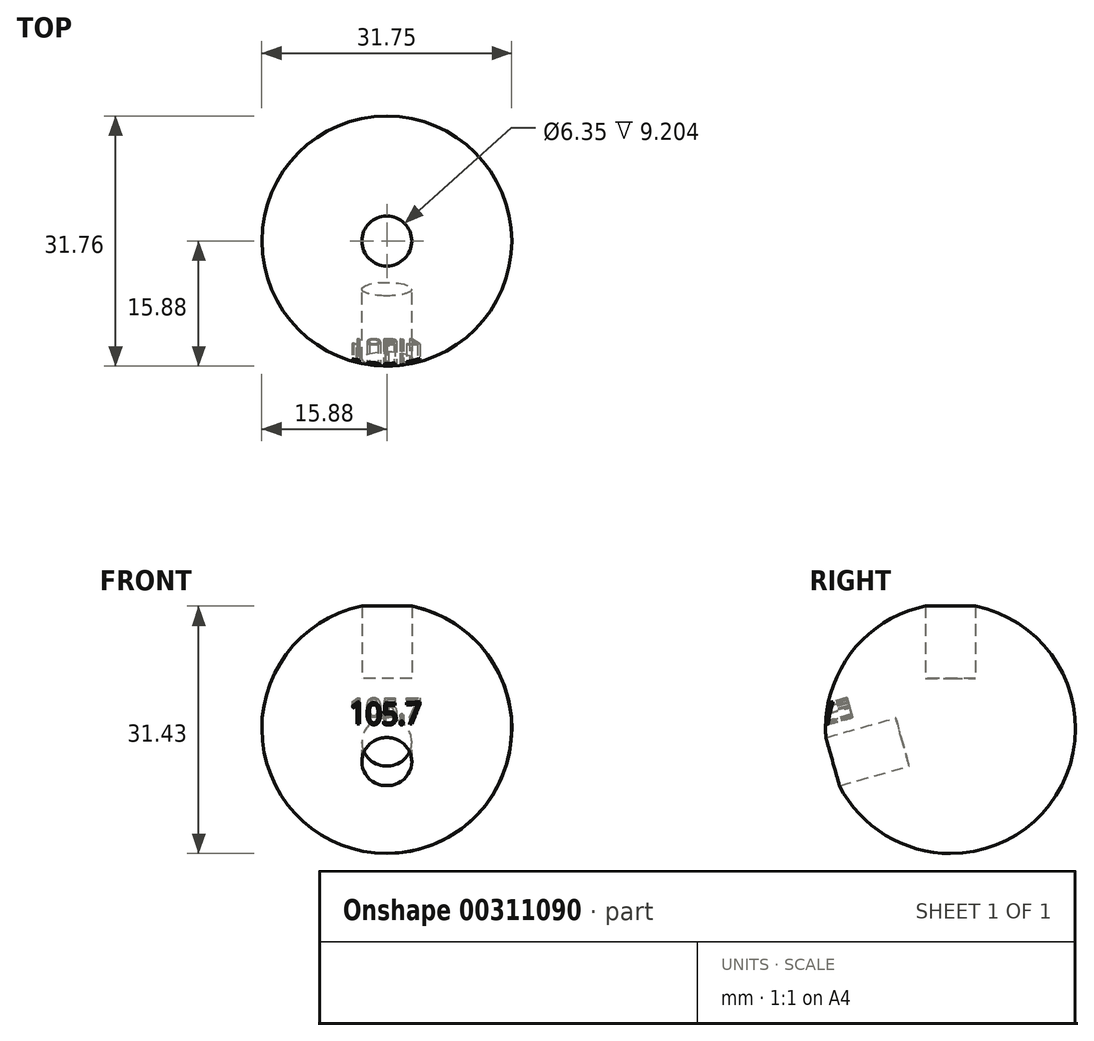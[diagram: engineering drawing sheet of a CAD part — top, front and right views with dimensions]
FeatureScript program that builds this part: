
annotation { "Feature Type Name" : "Feature", "Feature Type Description" : "" }
export const myFeature = defineFeature(function(context is Context, id is Id, definition is map)
    precondition{}
    {
        {
            var Q0;
            Q0=qCreatedBy(makeId("Front.planeOp"),FACE);
            var sketch = newSketch(context, id + "F0", { "sketchPlane" : qUnion([Q0])});
            skArc(sketch, "E0", {"start": v(0, 15.88) * mm, "mid": v(-15.88, 0) * mm, "end": v(0, -15.88) * mm});
            skLineSegment(sketch, "E1", {"start": v(0, 15.88) * mm, "end": v(0, -15.88) * mm});
            skSolve(sketch);
        }
        {
            var Q0;
            Q0=qCreatedBy(makeId("Top.planeOp"),FACE);
            var sketch = newSketch(context, id + "F1", { "sketchPlane" : qUnion([Q0])});
            skCircle(sketch, "E2", {"center": v(0, 0) * mm, "radius": 15.88 * mm});
            skSolve(sketch);
        }
        {
            var Q0;
            Q0=makeQuery(id+"F0.imprint","IMPRINT",FACE,{"disambiguationData":[TD([[makeQuery(id+"F0.imprint","IMPRINT",EDGE,{"derivedFrom":sQuery(id+"F0.wireOp",EDGE,"E0")}),1.0]])]});
            var Q1;
            Q1=sQuery(id+"F1.wireOp",EDGE,"E2");
            revolve(context, id + "F2", {"entities" : qUnion([Q0]), "axis" : qUnion([Q1]), "revolveType" : RevolveType.FULL});
        }
        {
            var Q0;
            Q0=qCreatedBy(makeId("Top.planeOp"),FACE);
            cPlane(context, id + "F3", {"entities" : qUnion([Q0]), "cplaneType" : CPlaneType.OFFSET, "offset" : 6.35 * mm, "width" : 152.4 * mm, "height" : 152.4 * mm});
        }
        {
            var Q0;
            Q0=qCreatedBy(id+"F3.planeOp",FACE);
            var sketch = newSketch(context, id + "F4", { "sketchPlane" : qUnion([Q0])});
            skCircle(sketch, "E3", {"center": v(0, 0) * mm, "radius": 3.18 * mm});
            skSolve(sketch);
        }
        {
            var Q0;
            Q0=qSketchRegion(id+"F4",true);
            extrude(context, id + "F5", {"entities" : qUnion([Q0]), "depth" : 50.8 * mm});
        }
        {
            var Q0;
            Q0=qCreatedBy(makeId("Top.planeOp"),FACE);
            var sketch = newSketch(context, id + "F6", { "sketchPlane" : qUnion([Q0])});
            skLineSegment(sketch, "E4", {"start": v(0, 0) * mm, "end": v(66.9, 0) * mm, "construction": true});
            skSolve(sketch);
        }
        {
            var Q0;
            Q0=makeQuery(id+"F5.opExtrude","SWEPT_BODY",BODY,{"disambiguationData":[OSD([sQuery(id+"F4.wireOp",EDGE,"E3")])]});
            var Q1;
            Q1=sQuery(id+"F6.wireOp",EDGE,"E4");
            transform(context, id + "F7", {"entities" : qUnion([Q0]), "transformType" : TransformType.ROTATION, "transformAxis" : qUnion([Q1]), "angle" : 105.7 * degree, "makeCopy" : true});
        }
        {
            var Q0;
            Q0=makeQuery(id+"F7.opPattern","COPY",FACE,{"derivedFrom":makeQuery(id+"F5.opExtrude","CAP_FACE",FACE,{"disambiguationData":[OSD([sQuery(id+"F4.wireOp",EDGE,"E3")])],"isStart":false}),"instanceName":"1"});
            cPlane(context, id + "F8", {"entities" : qUnion([Q0]), "cplaneType" : CPlaneType.OFFSET, "offset" : 25.4 * mm, "oppositeDirection" : true, "width" : 152.4 * mm, "height" : 152.4 * mm});
        }
        {
            var Q0;
            Q0=qCreatedBy(id+"F8.planeOp",FACE);
            var sketch = newSketch(context, id + "F9", { "sketchPlane" : qUnion([Q0])});
            skText(sketch, "E5", { "text": "105.7\n", "fontName": "OpenSans-Regular.ttf"});
            const initialGuessF9  = {"E5": [-0.00473, 0.00475, 1, 0, 0.00258]};
            skSetInitialGuess(sketch, initialGuessF9);
            skSolve(sketch);
        }
        {
            var Q0;
            Q0 = qSketchRegion(id + "F9", true);
            extrude(context, id + "F10", {"entities" : qUnion([Q0]), "operationType" : NewBodyOperationType.REMOVE, "oppositeDirection" : true, "depth" : 20.14 * mm});
        }
        {
            var Q0;
            Q0=makeQuery(id+"F5.opExtrude","SWEPT_BODY",BODY,{"disambiguationData":[OSD([sQuery(id+"F4.wireOp",EDGE,"E3")])]});
            var Q1;
            Q1=makeQuery(id+"F7.opPattern","COPY",BODY,{"derivedFrom":makeQuery(id+"F5.opExtrude","SWEPT_BODY",BODY,{"disambiguationData":[OSD([sQuery(id+"F4.wireOp",EDGE,"E3")])]}),"instanceName":"1"});
            var Q2;
            Q2=makeQuery(id+"F2.opRevolve","SWEPT_BODY",BODY,{"disambiguationData":[OSD([sQuery(id+"F0.wireOp",EDGE,"E0"),sQuery(id+"F0.wireOp",EDGE,"E1")])]});
            booleanBodies(context, id + "F11", {"operationType" : BooleanOperationType.SUBTRACTION, "tools" : qUnion([Q0, Q1]), "targets" : qUnion([Q2])});
        }
    });
